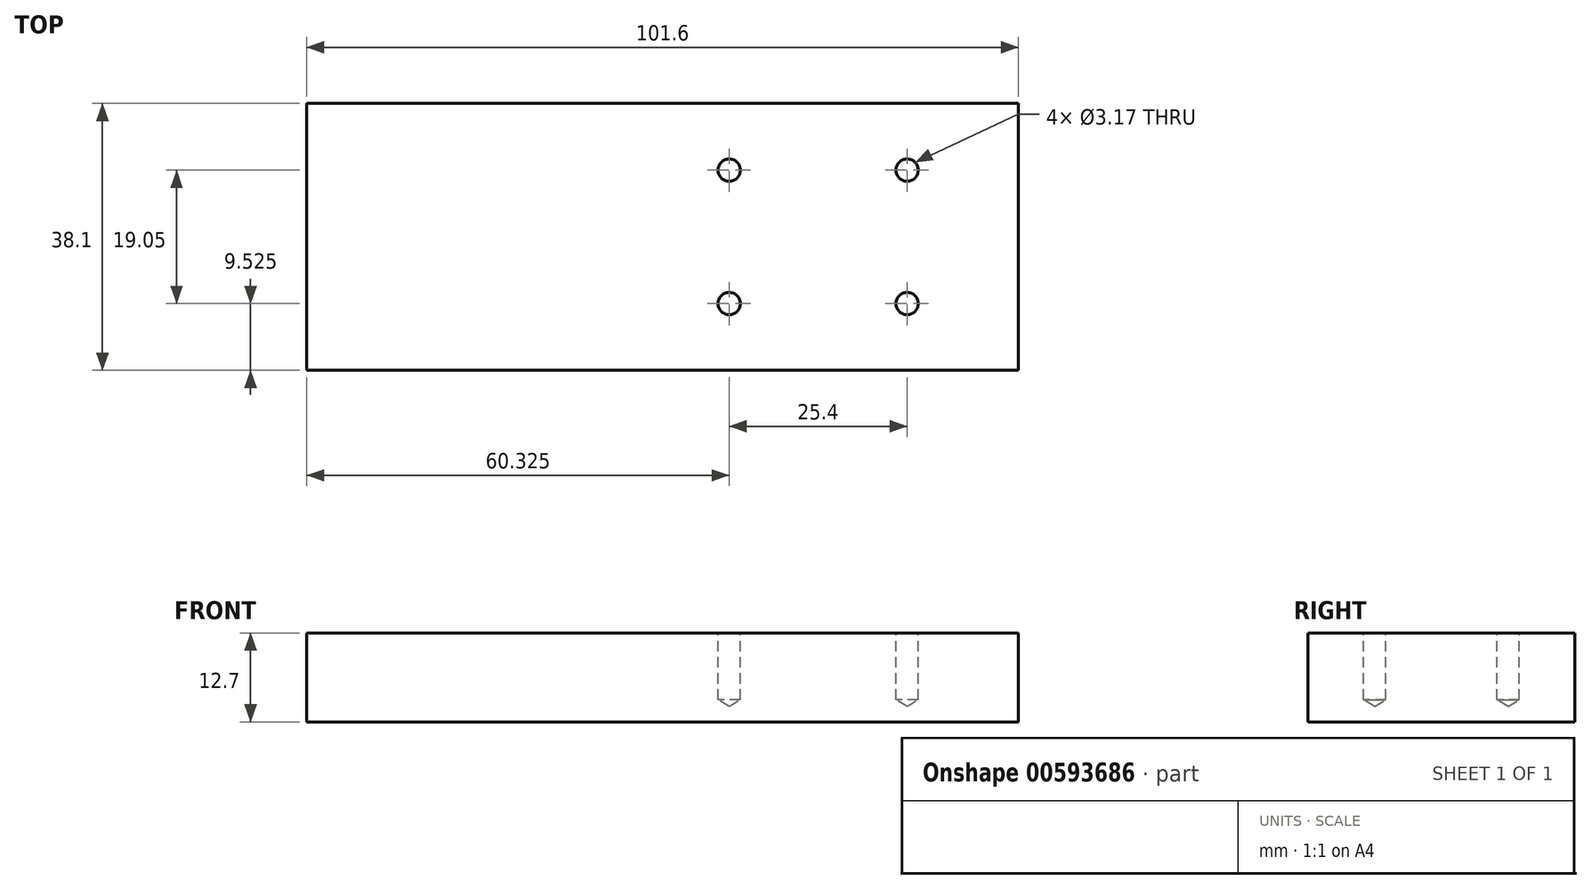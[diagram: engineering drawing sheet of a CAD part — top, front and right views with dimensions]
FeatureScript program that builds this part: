
annotation { "Feature Type Name" : "Feature", "Feature Type Description" : "" }
export const myFeature = defineFeature(function(context is Context, id is Id, definition is map)
    precondition{}
    {
        {
            var Q0;
            Q0=qCreatedBy(makeId("Top.planeOp"),FACE);
            var sketch = newSketch(context, id + "F0", { "sketchPlane" : qUnion([Q0])});
            skLineSegment(sketch, "E0.bottom", {"start": v(-50.8, 19.05) * mm, "end": v(50.8, 19.05) * mm});
            skLineSegment(sketch, "E0.top", {"start": v(-50.8, -19.05) * mm, "end": v(50.8, -19.05) * mm});
            skLineSegment(sketch, "E0.left", {"start": v(-50.8, 19.05) * mm, "end": v(-50.8, -19.05) * mm});
            skLineSegment(sketch, "E0.right", {"start": v(50.8, 19.05) * mm, "end": v(50.8, -19.05) * mm});
            skPoint(sketch, "E0.middle", {"position": v(0, 0) * mm});
            skSolve(sketch);
        }
        {
            var Q0;
            Q0=makeQuery(id+"F0.imprint","IMPRINT",FACE,{"disambiguationData":[TD([[makeQuery(id+"F0.imprint","IMPRINT",EDGE,{"derivedFrom":sQuery(id+"F0.wireOp",EDGE,"E0.bottom")}),-1.0]])]});
            extrude(context, id + "F1", {"entities" : qUnion([Q0]), "depth" : 12.7 * mm, "offsetDistance" : 25.4 * mm});
        }
        {
            var Q0;
            Q0=makeQuery(id+"F1.opExtrude","CAP_FACE",FACE,{"disambiguationData":[OSD([sQuery(id+"F0.wireOp",EDGE,"E0.bottom"),sQuery(id+"F0.wireOp",EDGE,"E0.top"),sQuery(id+"F0.wireOp",EDGE,"E0.left"),sQuery(id+"F0.wireOp",EDGE,"E0.right")])],"isStart":false});
            var sketch = newSketch(context, id + "F2", { "sketchPlane" : qUnion([Q0])});
            skLineSegment(sketch, "E1.bottom", {"start": v(34.93, 9.53) * mm, "end": v(9.53, 9.53) * mm, "construction": true});
            skLineSegment(sketch, "E1.top", {"start": v(34.93, -9.52) * mm, "end": v(9.53, -9.52) * mm, "construction": true});
            skLineSegment(sketch, "E1.left", {"start": v(34.93, 9.53) * mm, "end": v(34.93, -9.53) * mm, "construction": true});
            skLineSegment(sketch, "E1.right", {"start": v(9.53, 9.53) * mm, "end": v(9.53, -9.53) * mm, "construction": true});
            skPoint(sketch, "E1.middle", {"position": v(22.23, 0) * mm});
            skSolve(sketch);
        }
        {
            var Q0;
            Q0=sQuery(id+"F2.wireOp",VERTEX,"E1.right.start");
            var Q1;
            Q1=sQuery(id+"F2.wireOp",VERTEX,"E1.left.start");
            var Q2;
            Q2=sQuery(id+"F2.wireOp",VERTEX,"E1.left.end");
            var Q3;
            Q3=sQuery(id+"F2.wireOp",VERTEX,"E1.top.end");
            var Q4;
            Q4=makeQuery(id+"F1.opExtrude","SWEPT_BODY",BODY,{"disambiguationData":[OSD([sQuery(id+"F0.wireOp",EDGE,"E0.bottom"),sQuery(id+"F0.wireOp",EDGE,"E0.top"),sQuery(id+"F0.wireOp",EDGE,"E0.left"),sQuery(id+"F0.wireOp",EDGE,"E0.right")])]});
            hole(context, id + "F3", {"style" : HoleStyle.SIMPLE, "endStyle" : HoleEndStyle.BLIND, "holeDiameter" : 3.17 * mm, "majorDiameter" : 6.35 * mm, "holeDepth" : 9.52 * mm, "isTappedThrough" : true, "tappedDepth" : 12.7 * mm, "tapClearance" : 3, "locations" : qUnion([Q0, Q1, Q2, Q3]), "scope" : qUnion([Q4])});
        }
    });
